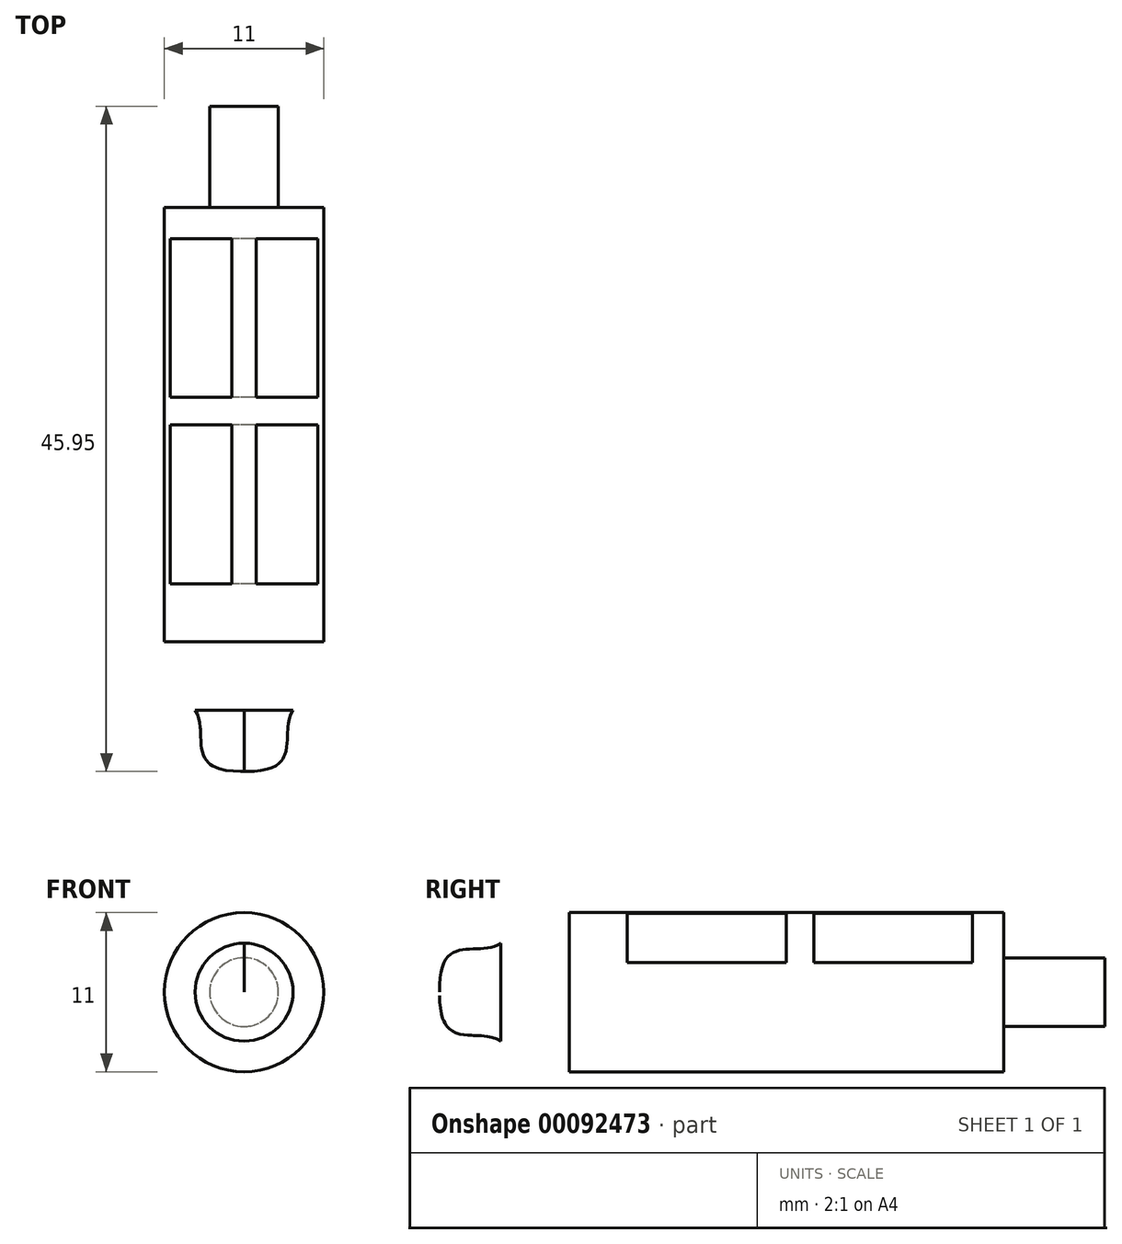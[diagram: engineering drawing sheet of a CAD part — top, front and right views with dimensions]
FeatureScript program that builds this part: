
annotation { "Feature Type Name" : "Feature", "Feature Type Description" : "" }
export const myFeature = defineFeature(function(context is Context, id is Id, definition is map)
    precondition{}
    {
        {
            var Q0;
            Q0=qCreatedBy(makeId("Right.planeOp"),FACE);
            var sketch = newSketch(context, id + "F0", { "sketchPlane" : qUnion([Q0])});
            skLineSegment(sketch, "E0.bottom", {"start": v(15, -5.5) * mm, "end": v(-15, -5.5) * mm});
            skLineSegment(sketch, "E0.top", {"start": v(15, 5.5) * mm, "end": v(-15, 5.5) * mm});
            skLineSegment(sketch, "E0.left", {"start": v(15, -5.5) * mm, "end": v(15, 5.5) * mm});
            skLineSegment(sketch, "E0.right", {"start": v(-15, -5.5) * mm, "end": v(-15, 5.5) * mm});
            skPoint(sketch, "E0.middle", {"position": v(0, 0) * mm});
            skLineSegment(sketch, "E1", {"start": v(-28.77, 0) * mm, "end": v(27.44, 0) * mm});
            skSolve(sketch);
        }
        {
            var Q0;
            {var subQ0=sQuery(id+"F0.wireOp",EDGE,"E0.bottom");Q0=makeQuery(id+"F0.imprint","IMPRINT",FACE,{"disambiguationData":[TD([[makeQuery(id+"F0.imprint","IMPRINT",EDGE,{"derivedFrom":subQ0}),-1.0]])]});}
            var Q1;
            Q1=sQuery(id+"F0.wireOp",EDGE,"E1");
            revolve(context, id + "F1", {"entities" : qUnion([Q0]), "axis" : qUnion([Q1]), "revolveType" : RevolveType.FULL});
        }
        {
            var Q0;
            Q0=qCreatedBy(makeId("Front.planeOp"),FACE);
            var sketch = newSketch(context, id + "F2", { "sketchPlane" : qUnion([Q0])});
            skCircle(sketch, "E2", {"center": v(0, 0) * mm, "radius": 2.38 * mm});
            skSolve(sketch);
        }
        {
            var Q0;
            Q0 = qSketchRegion(id + "F2", true);
            extrude(context, id + "F3", {"entities" : qUnion([Q0]), "operationType" : NewBodyOperationType.ADD, "oppositeDirection" : true, "depth" : 22 * mm});
        }
        {
            var Q0;
            Q0=qCreatedBy(makeId("Right.planeOp"),FACE);
            var sketch = newSketch(context, id + "F4", { "sketchPlane" : qUnion([Q0])});
            skLineSegment(sketch, "E3", {"start": v(-19.72, 3.38) * mm, "end": v(-19.72, 0) * mm});
            skLineSegment(sketch, "E4", {"start": v(-19.72, 0) * mm, "end": v(-23.94, 0) * mm});
            skFitSpline(sketch, "E5", {"points": [v(-23.94, 0) * mm, v(-19.72, 3.38) * mm], "startDerivative": vector(-0.33, 12.93) * mm, "endDerivative": vector(4.81, 3.17) * mm});
            skSolve(sketch);
        }
        {
            var Q0;
            Q0=makeQuery(id+"F4.imprint","IMPRINT",FACE,{"disambiguationData":[TD([[makeQuery(id+"F4.imprint","IMPRINT",EDGE,{"derivedFrom":sQuery(id+"F4.wireOp",EDGE,"E3")}),-1.0]])]});
            var Q1;
            Q1=sQuery(id+"F0.wireOp",EDGE,"E1");
            revolve(context, id + "F5", {"entities" : qUnion([Q0]), "axis" : qUnion([Q1]), "revolveType" : RevolveType.FULL});
        }
        {
            var Q0;
            Q0=qCreatedBy(makeId("Right.planeOp"),FACE);
            var sketch = newSketch(context, id + "F6", { "sketchPlane" : qUnion([Q0])});
            skLineSegment(sketch, "E6.bottom", {"start": v(-11, 5.43) * mm, "end": v(0, 5.43) * mm});
            skLineSegment(sketch, "E6.top", {"start": v(-11, 2.05) * mm, "end": v(0, 2.05) * mm});
            skLineSegment(sketch, "E6.left", {"start": v(-11, 5.43) * mm, "end": v(-11, 2.05) * mm});
            skLineSegment(sketch, "E6.right", {"start": v(0, 5.43) * mm, "end": v(0, 2.05) * mm});
            skLineSegment(sketch, "E7.bottom", {"start": v(1.89, 5.43) * mm, "end": v(12.87, 5.43) * mm});
            skLineSegment(sketch, "E7.top", {"start": v(1.89, 2.05) * mm, "end": v(12.87, 2.05) * mm});
            skLineSegment(sketch, "E7.left", {"start": v(1.89, 5.43) * mm, "end": v(1.89, 2.05) * mm});
            skLineSegment(sketch, "E7.right", {"start": v(12.87, 5.43) * mm, "end": v(12.87, 2.05) * mm});
            skSolve(sketch);
        }
        {
            var Q0;
            Q0=makeQuery(id+"F6.imprint","IMPRINT",FACE,{"disambiguationData":[TD([[makeQuery(id+"F6.imprint","IMPRINT",EDGE,{"derivedFrom":sQuery(id+"F6.wireOp",EDGE,"E6.bottom")}),-1.0]])]});
            var Q1;
            Q1=makeQuery(id+"F6.imprint","IMPRINT",FACE,{"disambiguationData":[TD([[makeQuery(id+"F6.imprint","IMPRINT",EDGE,{"derivedFrom":sQuery(id+"F6.wireOp",EDGE,"E7.bottom")}),-1.0]])]});
            var Q2;
            Q2=sQuery(id+"F6.wireOp",EDGE,"E6.right");
            extrude(context, id + "F7", {"entities" : qUnion([Q0, Q1]), "operationType" : NewBodyOperationType.REMOVE, "surfaceEntities" : qUnion([Q2]), "depth" : 25 * mm, "symmetric" : true});
        }
    });
